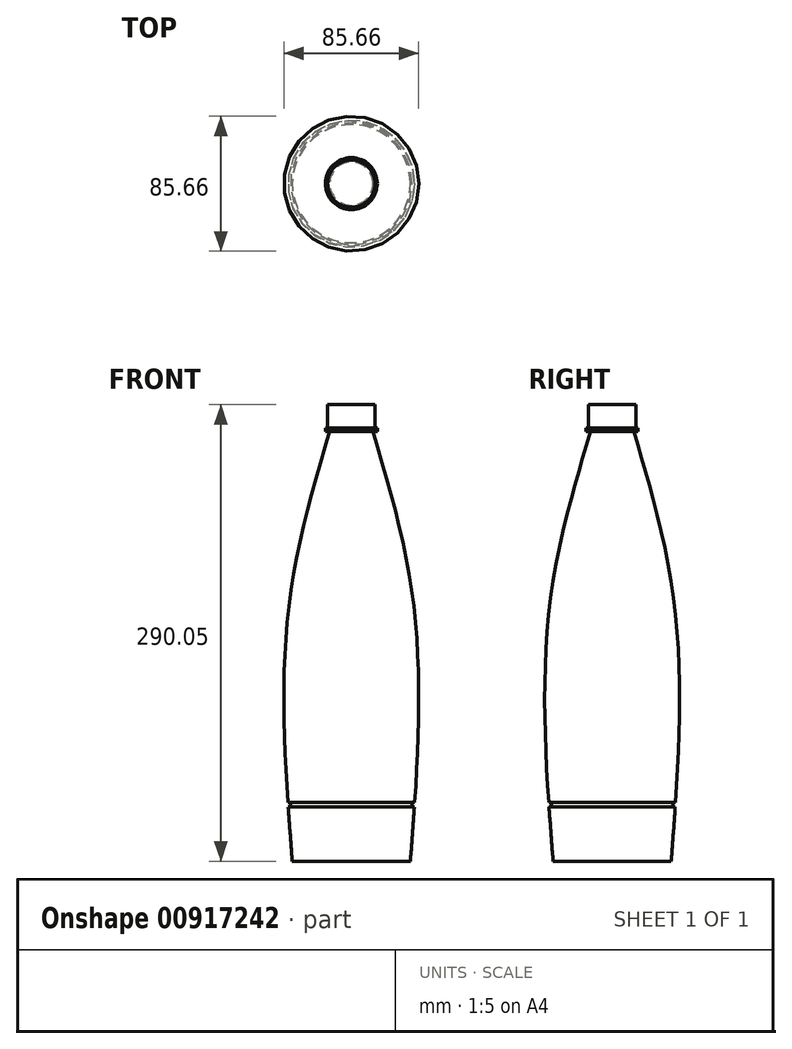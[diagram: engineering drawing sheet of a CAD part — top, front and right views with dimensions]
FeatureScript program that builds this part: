
annotation { "Feature Type Name" : "Feature", "Feature Type Description" : "" }
export const myFeature = defineFeature(function(context is Context, id is Id, definition is map)
    precondition{}
    {
        {
            var Q0;
            Q0=qCreatedBy(makeId("Top.planeOp"),FACE);
            var sketch = newSketch(context, id + "F0", { "sketchPlane" : qUnion([Q0])});
            skCircle(sketch, "E0", {"center": v(0, 0) * mm, "radius": 37.5 * mm});
            skSolve(sketch);
        }
        {
            var Q0;
            Q0=qCreatedBy(makeId("Top.planeOp"),FACE);
            cPlane(context, id + "F1", {"entities" : qUnion([Q0]), "cplaneType" : CPlaneType.OFFSET, "offset" : 177.8 * mm, "width" : 152.4 * mm, "height" : 152.4 * mm});
        }
        {
            var Q0;
            Q0=qCreatedBy(id+"F1.planeOp",FACE);
            var sketch = newSketch(context, id + "F2", { "sketchPlane" : qUnion([Q0])});
            skCircle(sketch, "E1", {"center": v(0, 0) * mm, "radius": 37.5 * mm});
            skSolve(sketch);
        }
        {
            var Q0;
            Q0=qCreatedBy(id+"F1.planeOp",FACE);
            cPlane(context, id + "F3", {"entities" : qUnion([Q0]), "cplaneType" : CPlaneType.OFFSET, "offset" : 95.25 * mm, "width" : 152.4 * mm, "height" : 152.4 * mm});
        }
        {
            var Q0;
            Q0=qCreatedBy(id+"F3.planeOp",FACE);
            var sketch = newSketch(context, id + "F4", { "sketchPlane" : qUnion([Q0])});
            skCircle(sketch, "E2", {"center": v(0, 0) * mm, "radius": 13.75 * mm});
            skSolve(sketch);
        }
        {
            var Q0;
            Q0 = qSketchRegion(id + "F0", true);
            var Q1;
            Q1 = qSketchRegion(id + "F2", true);
            var Q2;
            Q2 = qSketchRegion(id + "F4", true);
            loft(context, id + "F5", {"sheetProfilesArray" : [{ "sheetProfileEntities" : qUnion([Q0]) }, { "sheetProfileEntities" : qUnion([Q1]) }, { "sheetProfileEntities" : qUnion([Q2]) }]});
        }
        {
            var Q0;
            Q0=makeQuery(id+"F5.opLoft","CAP_FACE",FACE,{"disambiguationData":[OSD([makeQuery(id+"F4.imprint","IMPRINT",FACE,{"disambiguationData":[TD([[makeQuery(id+"F4.imprint","IMPRINT",EDGE,{"derivedFrom":sQuery(id+"F4.wireOp",EDGE,"E2")}),1.0]])]})])],"isStart":true});
            var sketch = newSketch(context, id + "F6", { "sketchPlane" : qUnion([Q0])});
            skCircle(sketch, "E3", {"center": v(0, 0) * mm, "radius": 16.5 * mm});
            skSolve(sketch);
        }
        {
            var Q0;
            Q0 = qSketchRegion(id + "F6", true);
            extrude(context, id + "F7", {"entities" : qUnion([Q0]), "operationType" : NewBodyOperationType.ADD, "depth" : 2 * mm, "offsetDistance" : 25.4 * mm});
        }
        {
            var Q0;
            Q0=makeQuery(id+"F7.opExtrude","CAP_FACE",FACE,{"disambiguationData":[OSD([sQuery(id+"F6.wireOp",EDGE,"E3")])],"isStart":false});
            var sketch = newSketch(context, id + "F8", { "sketchPlane" : qUnion([Q0])});
            skCircle(sketch, "E4", {"center": v(0, 0) * mm, "radius": 15 * mm});
            skSolve(sketch);
        }
        {
            var Q0;
            Q0 = qSketchRegion(id + "F8", true);
            extrude(context, id + "F9", {"entities" : qUnion([Q0]), "operationType" : NewBodyOperationType.ADD, "depth" : 15 * mm, "offsetDistance" : 25.4 * mm});
        }
        {
            var Q0;
            Q0=qCreatedBy(makeId("Right.planeOp"),FACE);
            var sketch = newSketch(context, id + "F10", { "sketchPlane" : qUnion([Q0])});
            skFitSpline(sketch, "E5", {"points": [v(-13.75, 273.05) * mm, v(-23.07, 241.47) * mm, v(-49.29, 152.7) * mm, v(-42.12, 59.83) * mm, v(-37.5, 0) * mm]});
            skFitSpline(sketch, "E6", {"points": [v(37.5, 0) * mm, v(42.12, 59.83) * mm, v(49.29, 152.7) * mm, v(23.07, 241.47) * mm, v(13.75, 273.05) * mm]});
            skCircle(sketch, "E7", {"center": v(40.17, 36) * mm, "radius": 1.5 * mm});
            skLineSegment(sketch, "E8", {"start": v(0, 0) * mm, "end": v(0, 67) * mm, "construction": true});
            skSolve(sketch);
        }
        {
            var Q0;
            Q0 = qSketchRegion(id + "F10", true);
            var Q1;
            Q1=sQuery(id+"F10.wireOp",EDGE,"E8");
            revolve(context, id + "F11", {"operationType" : NewBodyOperationType.REMOVE, "surfaceOperationType" : NewSurfaceOperationType.NEW, "entities" : qUnion([Q0]), "axis" : qUnion([Q1]), "revolveType" : RevolveType.FULL, "oppositeDirection" : true});
        }
    });
